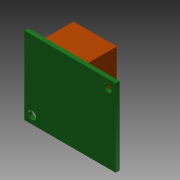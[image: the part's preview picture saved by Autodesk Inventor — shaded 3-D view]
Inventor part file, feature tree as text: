
AUTODESK INVENTOR PART (.ipt)
format: ipt  version: 2015 (Build 190159000, 159)  size: 99,840 bytes
history: native  units: mm
features: sketch x2, extrude x2
ambient origin geometry x8: Origin, YZ Plane, XZ Plane, XY Plane, X Axis, Y Axis, Z Axis, Center Point
bodies: Solid1 (feature_tree)
feature tree (4):
  sketch  "Sketch1"  dims[d0=39.751mm d1=33.655mm]
  extrude  "Extrusion1"  Depth=33.655mm
  extrude  "Extrusion2"  Depth=17.44mm
  sketch  "Sketch2"  dims[d2=3.5mm d3=3.5mm d4=3.429mm d5=3.429mm d6=3.429mm d7=3.429mm d8=18.79mm d9=15.32mm d10=24.243896mm d11=24.243896mm d12=1.7mm d13=0.0mm d14=17.44mm d15=0.0mm]
